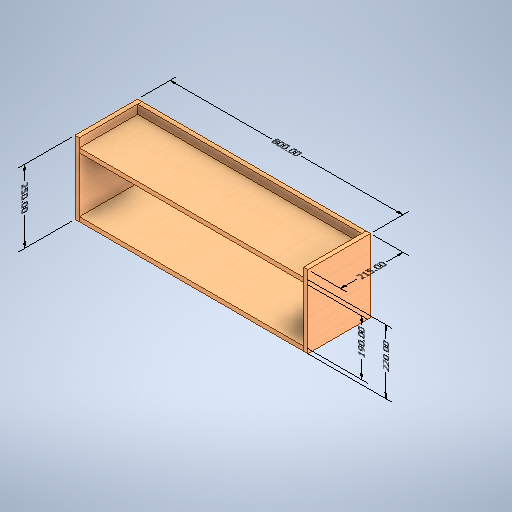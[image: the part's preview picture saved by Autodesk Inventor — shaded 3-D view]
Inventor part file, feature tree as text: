
AUTODESK INVENTOR PART (.ipt)
format: ipt  version: 2025.3 (Build 293356000, 356)  size: 359,936 bytes
history: native  units: mm
features: other x14, sketch x5, extrude x4, direct_edit x1, mirror x1, pattern_linear x1, move_body x1
ambient origin geometry x8: Origin, YZ Plane, XZ Plane, XY Plane, X Axis, Y Axis, Z Axis, Center Point
bodies: Body1 (feature_tree), Body2 (feature_tree), Body3 (feature_tree), Body4 (feature_tree), Body5 (feature_tree), Body6 (feature_tree)
feature tree (27):
  other  "ITEM1"
  other  "Annotations"
  sketch  "Sketch1"  dims[d0=800.0mm d1=250.0mm]
  sketch  "Sketch2"  dims[d2=800.0mm d3=200.0mm]
  sketch  "Sketch3"  dims[d4=15.0mm d5=200.0mm]
  extrude  "Extrusion1"  Depth=250.0mm
  direct_edit  "Direct Edit1"
  mirror  "Mirror1"
  extrude  "Extrusion2"  Depth=200.0mm
  pattern_linear  "Rectangular Pattern1"  Count1=20  [1 undecoded]
  sketch  "Sketch5"  dims[d8=200.0mm d9=0.0mm d10=20.0mm d12=205.0mm d13=0.0mm d14=0.0mm d15=15.0mm d16=90.0mm d17=90.0mm d18=15.0mm d19=0.0mm d20=15.0mm d21=0.0mm d22=250.0mm d23=3.925633mm d24=2.496534mm d25=800.0mm d26=0.0mm d27=10.0mm d28=215.0mm d29=9.556611mm d30=0.407419mm d31=190.0mm d32=0.34368mm d33=9.244926mm d34=220.0mm]
  extrude  "Extrusion3"  Depth=15.0mm
  extrude  "Extrusion4"  TaperAngle=0.0deg  [1 undecoded]
  other  "Pattern of ITEM1:1"
  other  "ITEM1A"
  sketch  "Sketch4"  dims[d6=0.0mm d7=15.0mm]
  other  "ITEM2"
  other  "Pattern of ITEM2:2"
  other  "ITEM2A"
  other  "ITEM3"
  other  "ITEM3A"
  move_body  "Move1"
  other  "Linear Dimension 1"
  other  "Linear Dimension 2"
  other  "Linear Dimension 3"
  other  "Linear Dimension 4"
  other  "Linear Dimension 5"
note: 2 required parameter values undecoded (feature->parameter linkage not recoverable at this tier; creation-order binding heuristic only, values carry confidence <= 0.55)
